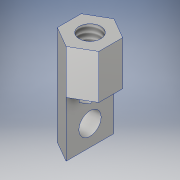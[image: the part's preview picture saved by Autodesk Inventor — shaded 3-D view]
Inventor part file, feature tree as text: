
AUTODESK INVENTOR PART (.ipt)
format: ipt  version: 2018 (Build 220112000, 112)  size: 139,776 bytes
history: native  units: in
note: dims shown in document units (in); Inventor stores cm internally (conversion verified against a paired STEP export)
features: sketch x4, extrude x2, hole x2
ambient origin geometry x8: Origin, YZ Plane, XZ Plane, XY Plane, X Axis, Y Axis, Z Axis, Center Point
bodies: Solid1 (feature_tree)
feature tree (8):
  extrude  "Extrusion1"  TaperAngle=90.0deg  [1 undecoded]
  hole  "Hole1"  [1 undecoded]
  extrude  "Extrusion2"  Depth=0.5in TaperAngle=0.0deg
  hole  "Hole2"  [1 undecoded]
  sketch  "Sketch1"  dims[d0=0.1875in d1=90.0deg]
  sketch  "Sketch2"  dims[d2=2.3622in d4=360.0deg d6=0.9in d7=0.0in]
  sketch  "Sketch3"  dims[d8=0.196in d9=0.25in d10=0.375in d11=0.25in d12=0.5635in d13=0.5in d14=0.8108in d15=0.5in d16=0.0in]
  sketch  "Sketch5"  dims[d17=0.1875in d18=0.266in d19=0.201in d20=0.5in d21=0.507in d22=0.25in d23=0.5635in d24=1.0in d25=0.8108in]
note: 3 required parameter values undecoded (feature->parameter linkage not recoverable at this tier; creation-order binding heuristic only, values carry confidence <= 0.55)
